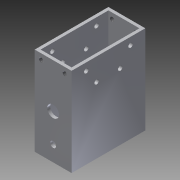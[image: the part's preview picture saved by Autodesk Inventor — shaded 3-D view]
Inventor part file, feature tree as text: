
AUTODESK INVENTOR PART (.ipt)
format: ipt  version: 2013 (Build 170138000, 138)  size: 185,856 bytes
history: native  units: mm
features: sketch x7, hole x5, thread x4, extrude x2, other x1
ambient origin geometry x1: Origin
feature tree (19):
  other  "ソリッド1"
  extrude  "押し出し1"  Depth=25.0mm
  extrude  "押し出し2"  Depth=50.0mm
  hole  "穴1"  [1 undecoded]
  hole  "穴2"  [1 undecoded]
  hole  "穴4"  [1 undecoded]
  thread  "ねじ1"
  thread  "ねじ2"
  thread  "ねじ3"
  thread  "ねじ4"
  hole  "穴5"  [1 undecoded]
  hole  "穴7"  [1 undecoded]
  sketch  "スケッチ1"
  sketch  "スケッチ2"
  sketch  "スケッチ3"
  sketch  "スケッチ4"
  sketch  "スケッチ5"
  sketch  "スケッチ7"
  sketch  "スケッチ8"
note: 5 required parameter values undecoded (feature->parameter linkage not recoverable at this tier; creation-order binding heuristic only, values carry confidence <= 0.55)
